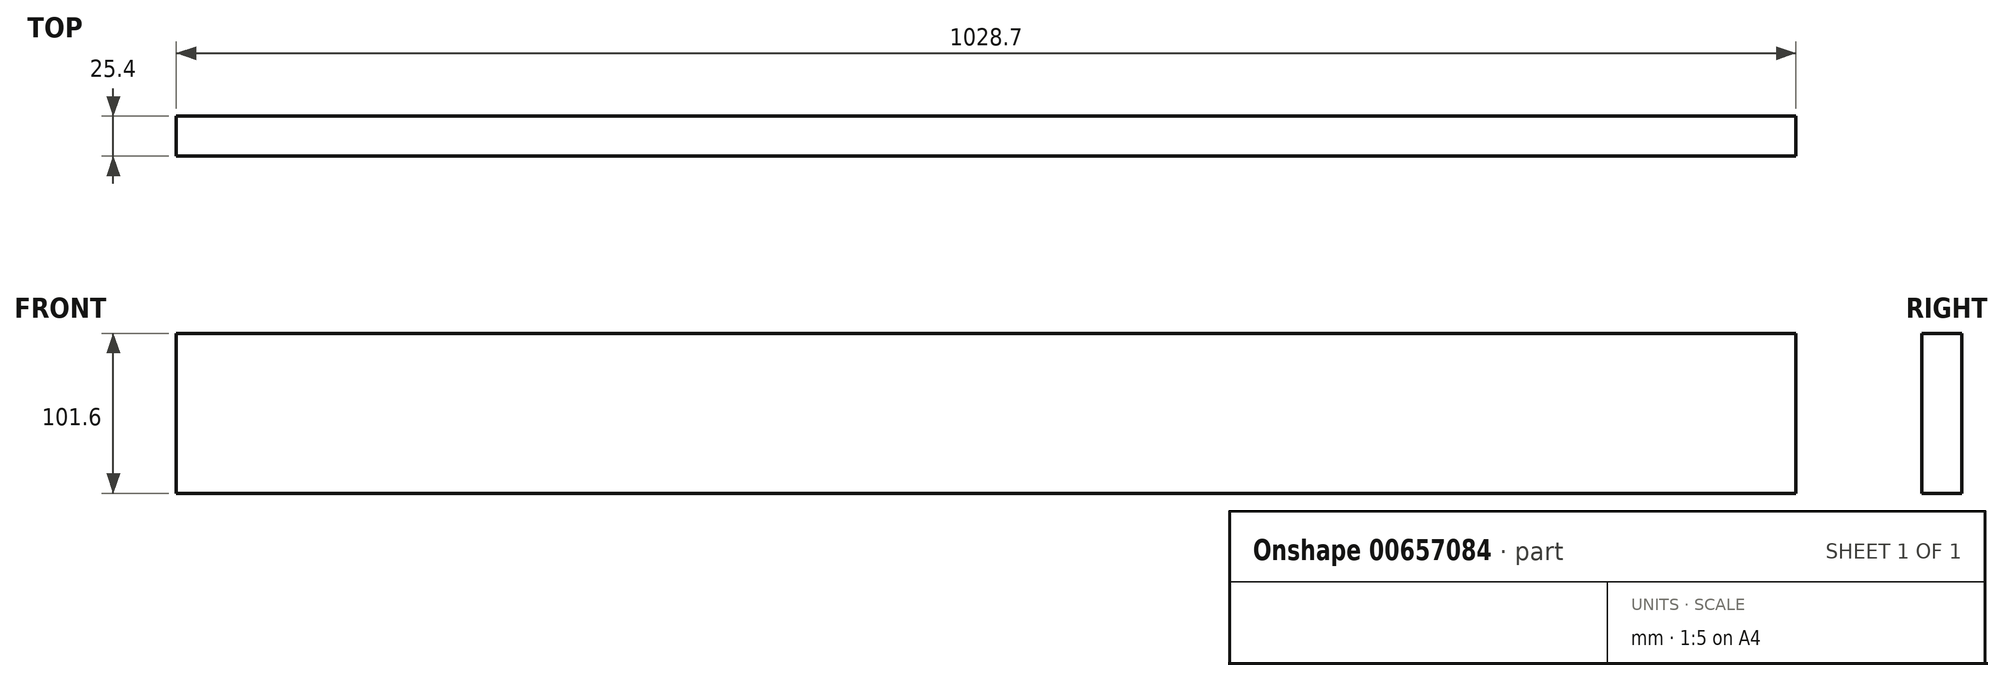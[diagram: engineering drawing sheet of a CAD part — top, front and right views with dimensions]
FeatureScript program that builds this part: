
annotation { "Feature Type Name" : "Feature", "Feature Type Description" : "" }
export const myFeature = defineFeature(function(context is Context, id is Id, definition is map)
    precondition{}
    {
        {
            var Q0;
            Q0=qCreatedBy(makeId("Right.planeOp"),FACE);
            var sketch = newSketch(context, id + "F0", { "sketchPlane" : qUnion([Q0])});
            skLineSegment(sketch, "E0.bottom", {"start": v(-29.17, 51.37) * mm, "end": v(-3.77, 51.37) * mm});
            skLineSegment(sketch, "E0.top", {"start": v(-29.17, -50.23) * mm, "end": v(-3.77, -50.23) * mm});
            skLineSegment(sketch, "E0.left", {"start": v(-29.17, 51.37) * mm, "end": v(-29.17, -50.23) * mm});
            skLineSegment(sketch, "E0.right", {"start": v(-3.77, 51.37) * mm, "end": v(-3.77, -50.23) * mm});
            skSolve(sketch);
        }
        {
            var Q0;
            Q0=makeQuery(id+"F0.imprint","IMPRINT",FACE,{"disambiguationData":[TD([[makeQuery(id+"F0.imprint","IMPRINT",EDGE,{"derivedFrom":sQuery(id+"F0.wireOp",EDGE,"E0.bottom")}),-1.0]])]});
            extrude(context, id + "F1", {"entities" : qUnion([Q0]), "depth" : 1028.7 * mm, "offsetDistance" : 25.4 * mm});
        }
    });
